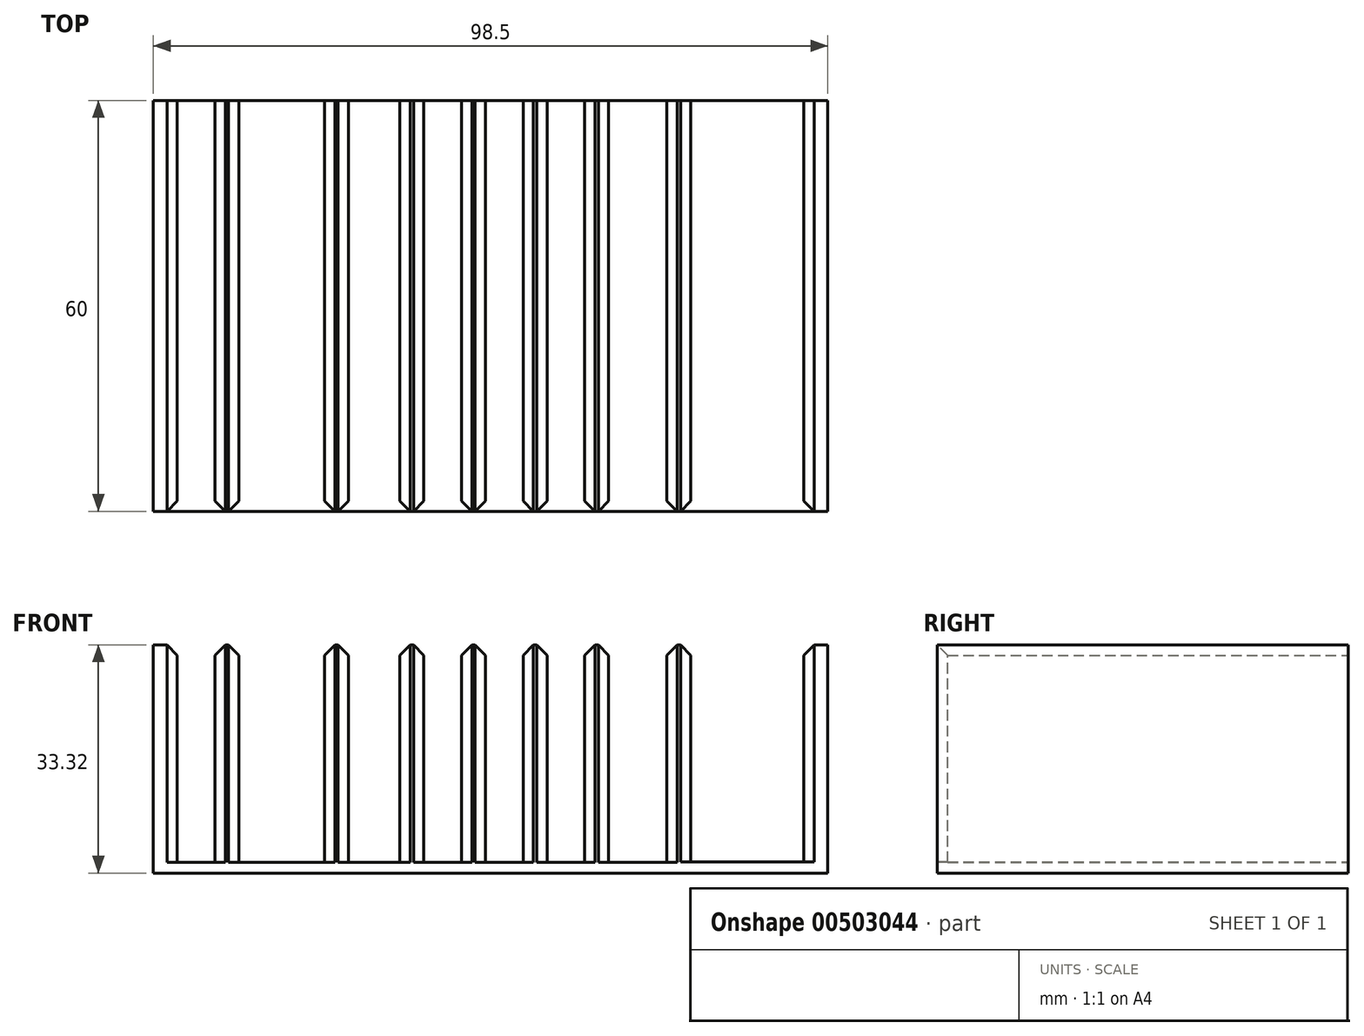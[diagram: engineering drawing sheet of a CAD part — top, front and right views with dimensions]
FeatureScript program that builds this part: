
annotation { "Feature Type Name" : "Feature", "Feature Type Description" : "" }
export const myFeature = defineFeature(function(context is Context, id is Id, definition is map)
    precondition{}
    {
        {
            var Q0;
            Q0=qCreatedBy(makeId("Front.planeOp"),FACE);
            var sketch = newSketch(context, id + "F0", { "sketchPlane" : qUnion([Q0])});
            skLineSegment(sketch, "E0", {"start": v(-57.5, -9.31) * mm, "end": v(41, -9.31) * mm});
            skLineSegment(sketch, "E1", {"start": v(41, -9.31) * mm, "end": v(41, 24) * mm});
            skLineSegment(sketch, "E2", {"start": v(41, 24) * mm, "end": v(37.5, 24) * mm});
            skLineSegment(sketch, "E3", {"start": v(37.5, 24) * mm, "end": v(37.5, -7.69) * mm});
            skLineSegment(sketch, "E4", {"start": v(37.5, -7.69) * mm, "end": v(21, -7.69) * mm});
            skLineSegment(sketch, "E5", {"start": v(21, -7.69) * mm, "end": v(21, 24) * mm});
            skLineSegment(sketch, "E6", {"start": v(21, 24) * mm, "end": v(17.5, 24) * mm});
            skLineSegment(sketch, "E7", {"start": v(17.5, 24) * mm, "end": v(17.5, -7.76) * mm});
            skLineSegment(sketch, "E8", {"start": v(17.5, -7.76) * mm, "end": v(9, -7.76) * mm});
            skLineSegment(sketch, "E9", {"start": v(9, -7.76) * mm, "end": v(9, 24) * mm});
            skLineSegment(sketch, "E10", {"start": v(9, 24) * mm, "end": v(5.5, 24) * mm});
            skLineSegment(sketch, "E11", {"start": v(5.5, 24) * mm, "end": v(5.5, -7.76) * mm});
            skLineSegment(sketch, "E12", {"start": v(5.5, -7.76) * mm, "end": v(0, -7.76) * mm});
            skLineSegment(sketch, "E13", {"start": v(0, -7.76) * mm, "end": v(0, 24) * mm});
            skLineSegment(sketch, "E14", {"start": v(0, 24) * mm, "end": v(-3.5, 24) * mm});
            skLineSegment(sketch, "E15", {"start": v(-3.5, 24) * mm, "end": v(-3.5, -7.76) * mm});
            skLineSegment(sketch, "E16", {"start": v(-3.5, -7.76) * mm, "end": v(-9, -7.76) * mm});
            skLineSegment(sketch, "E17", {"start": v(-9, -7.76) * mm, "end": v(-9, 24) * mm});
            skLineSegment(sketch, "E18", {"start": v(-9, 24) * mm, "end": v(-12.5, 24) * mm});
            skLineSegment(sketch, "E19", {"start": v(-12.5, 24) * mm, "end": v(-12.5, -7.76) * mm});
            skLineSegment(sketch, "E20", {"start": v(-12.5, -7.76) * mm, "end": v(-18, -7.76) * mm});
            skLineSegment(sketch, "E21", {"start": v(-18, -7.76) * mm, "end": v(-18, 24) * mm});
            skLineSegment(sketch, "E22", {"start": v(-18, 24) * mm, "end": v(-21.5, 24) * mm});
            skLineSegment(sketch, "E23", {"start": v(-21.5, 24) * mm, "end": v(-21.5, -7.76) * mm});
            skLineSegment(sketch, "E24", {"start": v(-21.5, -7.76) * mm, "end": v(-29, -7.76) * mm});
            skLineSegment(sketch, "E25", {"start": v(-29, -7.76) * mm, "end": v(-29, 24) * mm});
            skLineSegment(sketch, "E26", {"start": v(-29, 24) * mm, "end": v(-32.5, 24) * mm});
            skLineSegment(sketch, "E27", {"start": v(-32.5, 24) * mm, "end": v(-32.5, -7.76) * mm});
            skLineSegment(sketch, "E28", {"start": v(-32.5, -7.76) * mm, "end": v(-45, -7.76) * mm});
            skLineSegment(sketch, "E29", {"start": v(-45, -7.76) * mm, "end": v(-45, 24) * mm});
            skLineSegment(sketch, "E30", {"start": v(-45, 24) * mm, "end": v(-48.5, 24) * mm});
            skLineSegment(sketch, "E31", {"start": v(-48.5, 24) * mm, "end": v(-48.5, -7.76) * mm});
            skLineSegment(sketch, "E32", {"start": v(-48.5, -7.76) * mm, "end": v(-54, -7.76) * mm});
            skLineSegment(sketch, "E33", {"start": v(-54, -7.76) * mm, "end": v(-54, 24) * mm});
            skLineSegment(sketch, "E34", {"start": v(-57.5, -9.31) * mm, "end": v(-57.5, 24) * mm});
            skLineSegment(sketch, "E35", {"start": v(-57.5, 24) * mm, "end": v(-54, 24) * mm});
            skSolve(sketch);
        }
        {
            var Q0;
            Q0=makeQuery(id+"F0.imprint","IMPRINT",FACE,{"disambiguationData":[TD([[makeQuery(id+"F0.imprint","IMPRINT",EDGE,{"derivedFrom":sQuery(id+"F0.wireOp",EDGE,"E0")}),1.0]])]});
            extrude(context, id + "F1", {"entities" : qUnion([Q0]), "depth" : 60 * mm});
        }
        {
            var Q0;
            Q0=makeQuery(id+"F1.opExtrude","SWEPT_EDGE",EDGE,{"disambiguationData":[OSD([sQuery(id+"F0.wireOp",EDGE,"E2"),sQuery(id+"F0.wireOp",EDGE,"E3")])]});
            var Q1;
            Q1=makeQuery(id+"F1.opExtrude","SWEPT_EDGE",EDGE,{"disambiguationData":[OSD([sQuery(id+"F0.wireOp",EDGE,"E5"),sQuery(id+"F0.wireOp",EDGE,"E6")])]});
            var Q2;
            Q2=makeQuery(id+"F1.opExtrude","SWEPT_EDGE",EDGE,{"disambiguationData":[OSD([sQuery(id+"F0.wireOp",EDGE,"E6"),sQuery(id+"F0.wireOp",EDGE,"E7")])]});
            var Q3;
            Q3=makeQuery(id+"F1.opExtrude","SWEPT_EDGE",EDGE,{"disambiguationData":[OSD([sQuery(id+"F0.wireOp",EDGE,"E9"),sQuery(id+"F0.wireOp",EDGE,"E10")])]});
            var Q4;
            Q4=makeQuery(id+"F1.opExtrude","SWEPT_EDGE",EDGE,{"disambiguationData":[OSD([sQuery(id+"F0.wireOp",EDGE,"E10"),sQuery(id+"F0.wireOp",EDGE,"E11")])]});
            var Q5;
            Q5=makeQuery(id+"F1.opExtrude","SWEPT_EDGE",EDGE,{"disambiguationData":[OSD([sQuery(id+"F0.wireOp",EDGE,"E13"),sQuery(id+"F0.wireOp",EDGE,"E14")])]});
            var Q6;
            Q6=makeQuery(id+"F1.opExtrude","SWEPT_EDGE",EDGE,{"disambiguationData":[OSD([sQuery(id+"F0.wireOp",EDGE,"E14"),sQuery(id+"F0.wireOp",EDGE,"E15")])]});
            var Q7;
            Q7=makeQuery(id+"F1.opExtrude","SWEPT_EDGE",EDGE,{"disambiguationData":[OSD([sQuery(id+"F0.wireOp",EDGE,"E17"),sQuery(id+"F0.wireOp",EDGE,"E18")])]});
            var Q8;
            Q8=makeQuery(id+"F1.opExtrude","SWEPT_EDGE",EDGE,{"disambiguationData":[OSD([sQuery(id+"F0.wireOp",EDGE,"E18"),sQuery(id+"F0.wireOp",EDGE,"E19")])]});
            var Q9;
            Q9=makeQuery(id+"F1.opExtrude","SWEPT_EDGE",EDGE,{"disambiguationData":[OSD([sQuery(id+"F0.wireOp",EDGE,"E21"),sQuery(id+"F0.wireOp",EDGE,"E22")])]});
            var Q10;
            Q10=makeQuery(id+"F1.opExtrude","SWEPT_EDGE",EDGE,{"disambiguationData":[OSD([sQuery(id+"F0.wireOp",EDGE,"E22"),sQuery(id+"F0.wireOp",EDGE,"E23")])]});
            var Q11;
            Q11=makeQuery(id+"F1.opExtrude","SWEPT_EDGE",EDGE,{"disambiguationData":[OSD([sQuery(id+"F0.wireOp",EDGE,"E25"),sQuery(id+"F0.wireOp",EDGE,"E26")])]});
            var Q12;
            Q12=makeQuery(id+"F1.opExtrude","SWEPT_EDGE",EDGE,{"disambiguationData":[OSD([sQuery(id+"F0.wireOp",EDGE,"E26"),sQuery(id+"F0.wireOp",EDGE,"E27")])]});
            var Q13;
            Q13=makeQuery(id+"F1.opExtrude","SWEPT_EDGE",EDGE,{"disambiguationData":[OSD([sQuery(id+"F0.wireOp",EDGE,"E29"),sQuery(id+"F0.wireOp",EDGE,"E30")])]});
            var Q14;
            Q14=makeQuery(id+"F1.opExtrude","SWEPT_EDGE",EDGE,{"disambiguationData":[OSD([sQuery(id+"F0.wireOp",EDGE,"E30"),sQuery(id+"F0.wireOp",EDGE,"E31")])]});
            var Q15;
            Q15=makeQuery(id+"F1.opExtrude","SWEPT_EDGE",EDGE,{"disambiguationData":[OSD([sQuery(id+"F0.wireOp",EDGE,"E33"),sQuery(id+"F0.wireOp",EDGE,"E35")])]});
            var Q16;
            Q16=makeQuery(id+"F1.opExtrude","CAP_EDGE",EDGE,{"disambiguationData":[OSD([sQuery(id+"F0.wireOp",EDGE,"E9")])],"isStart":false});
            var Q17;
            Q17=makeQuery(id+"F1.opExtrude","CAP_EDGE",EDGE,{"disambiguationData":[OSD([sQuery(id+"F0.wireOp",EDGE,"E11")])],"isStart":false});
            var Q18;
            Q18=makeQuery(id+"F1.opExtrude","CAP_EDGE",EDGE,{"disambiguationData":[OSD([sQuery(id+"F0.wireOp",EDGE,"E3")])],"isStart":false});
            var Q19;
            Q19=makeQuery(id+"F1.opExtrude","CAP_EDGE",EDGE,{"disambiguationData":[OSD([sQuery(id+"F0.wireOp",EDGE,"E5")])],"isStart":false});
            var Q20;
            Q20=makeQuery(id+"F1.opExtrude","CAP_EDGE",EDGE,{"disambiguationData":[OSD([sQuery(id+"F0.wireOp",EDGE,"E7")])],"isStart":false});
            var Q21;
            Q21=makeQuery(id+"F1.opExtrude","CAP_EDGE",EDGE,{"disambiguationData":[OSD([sQuery(id+"F0.wireOp",EDGE,"E13")])],"isStart":false});
            var Q22;
            Q22=makeQuery(id+"F1.opExtrude","CAP_EDGE",EDGE,{"disambiguationData":[OSD([sQuery(id+"F0.wireOp",EDGE,"E15")])],"isStart":false});
            var Q23;
            Q23=makeQuery(id+"F1.opExtrude","CAP_EDGE",EDGE,{"disambiguationData":[OSD([sQuery(id+"F0.wireOp",EDGE,"E19")])],"isStart":false});
            var Q24;
            Q24=makeQuery(id+"F1.opExtrude","CAP_EDGE",EDGE,{"disambiguationData":[OSD([sQuery(id+"F0.wireOp",EDGE,"E21")])],"isStart":false});
            var Q25;
            Q25=makeQuery(id+"F1.opExtrude","CAP_EDGE",EDGE,{"disambiguationData":[OSD([sQuery(id+"F0.wireOp",EDGE,"E23")])],"isStart":false});
            var Q26;
            Q26=makeQuery(id+"F1.opExtrude","CAP_EDGE",EDGE,{"disambiguationData":[OSD([sQuery(id+"F0.wireOp",EDGE,"E25")])],"isStart":false});
            var Q27;
            Q27=makeQuery(id+"F1.opExtrude","CAP_EDGE",EDGE,{"disambiguationData":[OSD([sQuery(id+"F0.wireOp",EDGE,"E27")])],"isStart":false});
            var Q28;
            Q28=makeQuery(id+"F1.opExtrude","CAP_EDGE",EDGE,{"disambiguationData":[OSD([sQuery(id+"F0.wireOp",EDGE,"E29")])],"isStart":false});
            var Q29;
            Q29=makeQuery(id+"F1.opExtrude","CAP_EDGE",EDGE,{"disambiguationData":[OSD([sQuery(id+"F0.wireOp",EDGE,"E31")])],"isStart":false});
            var Q30;
            Q30=makeQuery(id+"F1.opExtrude","CAP_EDGE",EDGE,{"disambiguationData":[OSD([sQuery(id+"F0.wireOp",EDGE,"E33")])],"isStart":false});
            var Q31;
            Q31=makeQuery(id+"F1.opExtrude","CAP_EDGE",EDGE,{"disambiguationData":[OSD([sQuery(id+"F0.wireOp",EDGE,"E17")])],"isStart":false});
            chamfer(context, id + "F2", {"entities" : qUnion([Q0, Q1, Q2, Q3, Q4, Q5, Q6, Q7, Q8, Q9, Q10, Q11, Q12, Q13, Q14, Q15, Q16, Q17, Q18, Q19, Q20, Q21, Q22, Q23, Q24, Q25, Q26, Q27, Q28, Q29, Q30, Q31]), "width" : 1.5 * mm, "tangentPropagation" : true});
        }
    });
